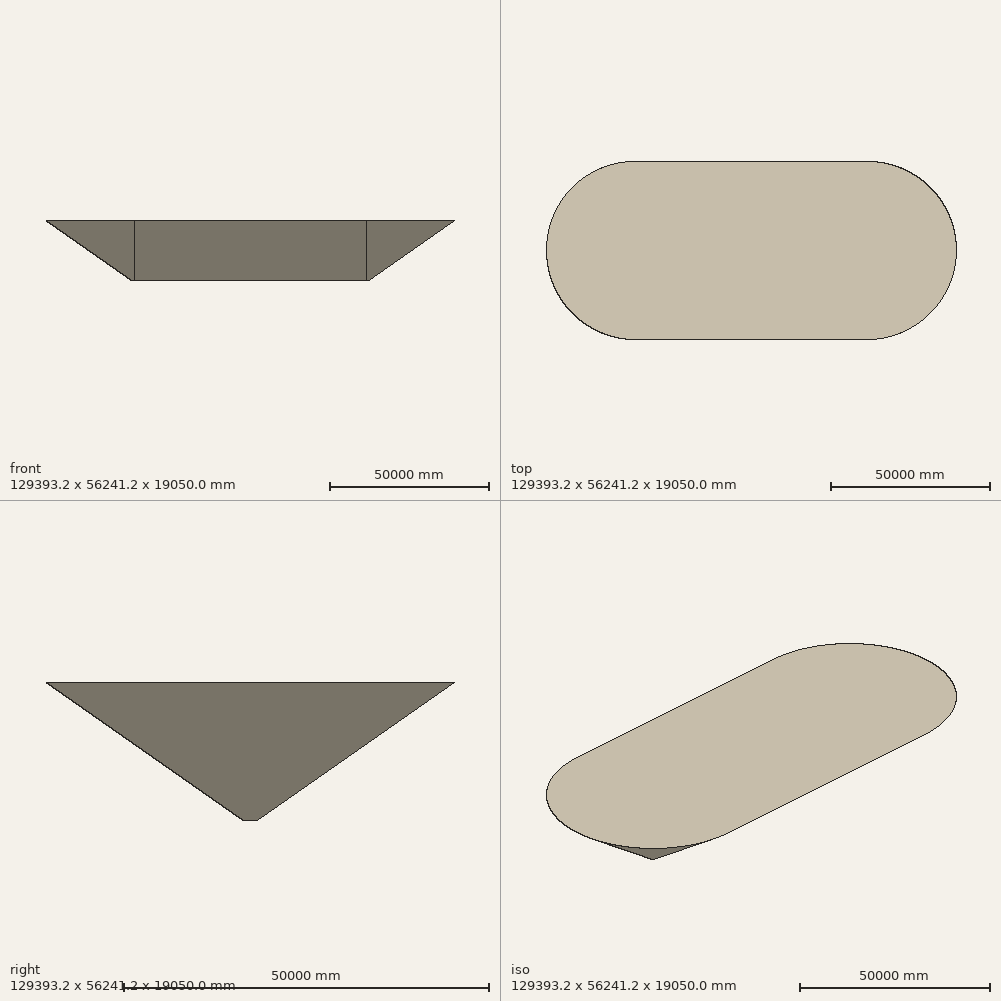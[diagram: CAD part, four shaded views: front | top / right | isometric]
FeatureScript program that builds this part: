
annotation { "Feature Type Name" : "Feature", "Feature Type Description" : "" }
export const myFeature = defineFeature(function(context is Context, id is Id, definition is map)
    precondition{}
    {
        {
            var Q0;
            Q0=qCreatedBy(makeId("Top.planeOp"),FACE);
            var sketch = newSketch(context, id + "F0", { "sketchPlane" : qUnion([Q0])});
            skLineSegment(sketch, "E0.bottom", {"start": v(-45720, 914.4) * mm, "end": v(27432, 914.4) * mm});
            skLineSegment(sketch, "E0.top", {"start": v(-45720, -914.4) * mm, "end": v(27432, -914.4) * mm});
            skArc(sketch, "E1", {"start": v(-45720, 914.4) * mm, "mid": v(-46634.4, 0) * mm, "end": v(-45720, -914.4) * mm});
            skArc(sketch, "E2", {"start": v(27432, 914.4) * mm, "mid": v(28346.4, 0) * mm, "end": v(27432, -914.4) * mm});
            skSolve(sketch);
        }
        {
            var Q0;
            Q0=makeQuery(id+"F0.imprint","IMPRINT",FACE,{"disambiguationData":[TD([[makeQuery(id+"F0.imprint","IMPRINT",EDGE,{"derivedFrom":sQuery(id+"F0.wireOp",EDGE,"E0.bottom")}),-1.0]])]});
            extrude(context, id + "F1", {"entities" : qUnion([Q0]), "depth" : 19050 * mm, "hasDraft" : true, "draftAngle" : 55 * degree});
        }
    });
